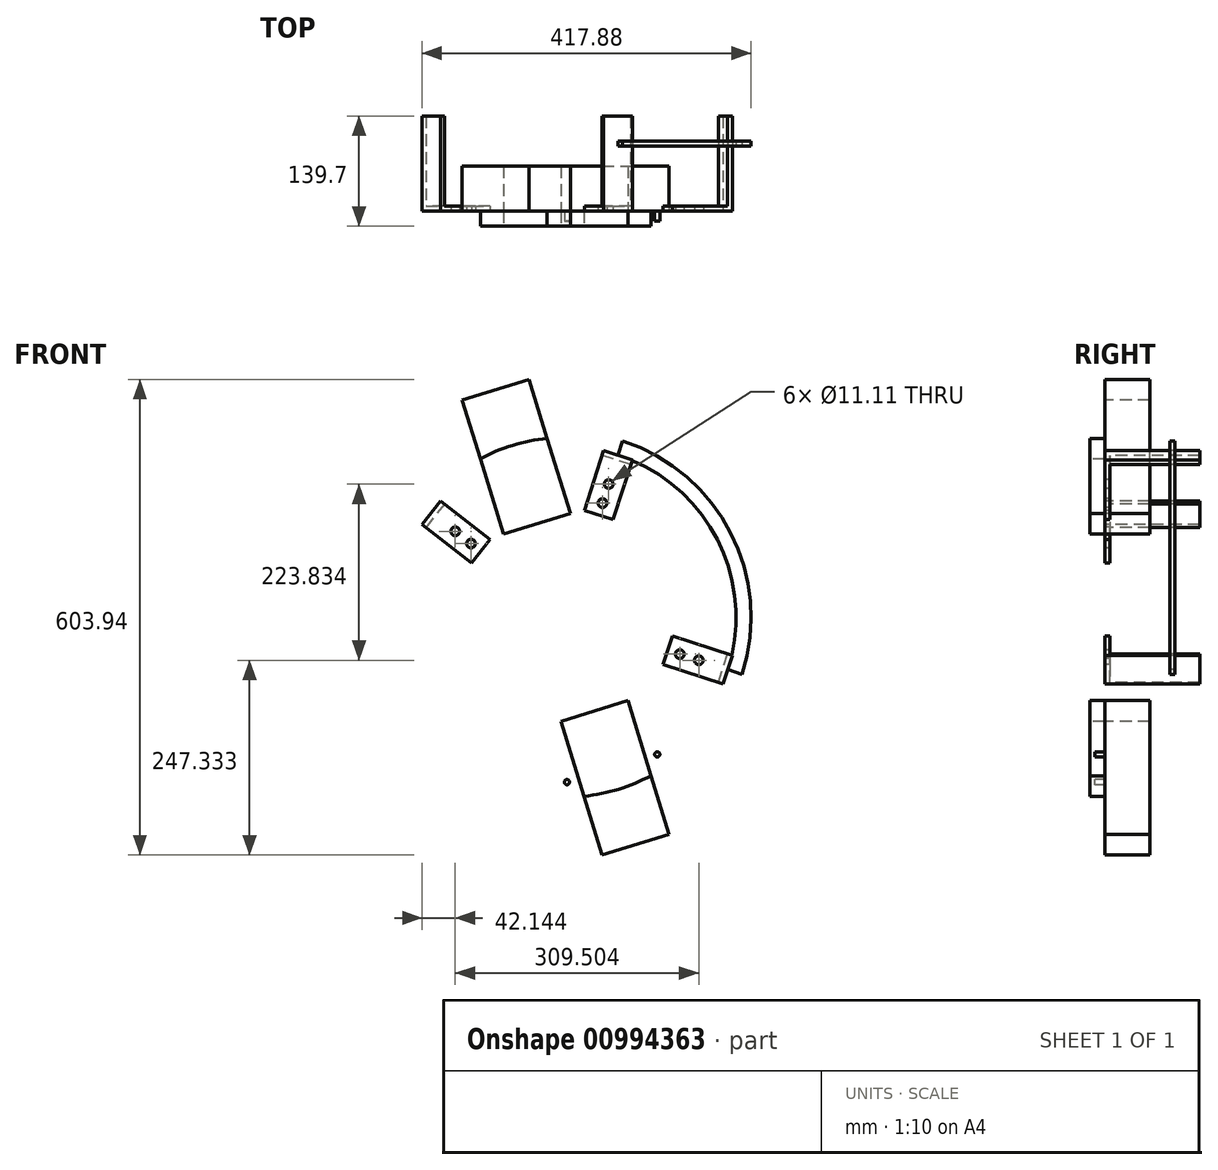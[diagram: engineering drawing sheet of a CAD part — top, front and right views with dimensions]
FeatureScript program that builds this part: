
annotation { "Feature Type Name" : "Feature", "Feature Type Description" : "" }
export const myFeature = defineFeature(function(context is Context, id is Id, definition is map)
    precondition{}
    {
        {
            var Q0;
            Q0=qCreatedBy(makeId("Front.planeOp"),FACE);
            var sketch = newSketch(context, id + "F0", { "sketchPlane" : qUnion([Q0])});
            skCircle(sketch, "E0", {"center": v(0, 0) * mm, "radius": 228.6 * mm});
            skSolve(sketch);
        }
        {
            var Q0;
            Q0=qSketchRegion(id+"F0",true);
            extrude(context, id + "F1", {"entities" : qUnion([Q0]), "depth" : 19.05 * mm, "offsetDistance" : 25.4 * mm});
        }
        {
            var Q0;
            Q0=makeQuery(id+"F1.opExtrude","CAP_FACE",FACE,{"disambiguationData":[OSD([sQuery(id+"F0.wireOp",EDGE,"E0")])],"isStart":false});
            var sketch = newSketch(context, id + "F2", { "sketchPlane" : qUnion([Q0])});
            skCircle(sketch, "E1", {"center": v(0, 0) * mm, "radius": 38.1 * mm});
            skSolve(sketch);
        }
        {
            var Q0;
            Q0=makeQuery(id+"F2.imprint","IMPRINT",FACE,{"disambiguationData":[TD([[makeQuery(id+"F2.imprint","IMPRINT",EDGE,{"derivedFrom":sQuery(id+"F2.wireOp",EDGE,"E1")}),1.0]])]});
            extrude(context, id + "F3", {"entities" : qUnion([Q0]), "operationType" : NewBodyOperationType.REMOVE, "endBound" : BoundingType.THROUGH_ALL, "oppositeDirection" : true, "depth" : 25.4 * mm, "offsetDistance" : 25.4 * mm});
        }
        {
            var Q0;
            Q0=makeQuery(id+"F1.opExtrude","CAP_FACE",FACE,{"disambiguationData":[OSD([sQuery(id+"F0.wireOp",EDGE,"E0")])],"isStart":false});
            var sketch = newSketch(context, id + "F4", { "sketchPlane" : qUnion([Q0])});
            skLineSegment(sketch, "E2", {"start": v(0, 0) * mm, "end": v(-180.4, 140.41) * mm, "construction": true});
            skCircle(sketch, "E3", {"center": v(-120.26, 93.6) * mm, "radius": 4.76 * mm});
            skCircle(sketch, "E4", {"center": v(-140.3, 109.21) * mm, "radius": 4.76 * mm});
            skLineSegment(sketch, "E5", {"start": v(0, 0) * mm, "end": v(-67.23, 218.49) * mm, "construction": true});
            skCircle(sketch, "E6", {"center": v(-116.36, 174.14) * mm, "radius": 3.3 * mm});
            skCircle(sketch, "E7", {"center": v(-1.67, 209.43) * mm, "radius": 3.3 * mm});
            skLineSegment(sketch, "E8", {"start": v(-1.67, 209.43) * mm, "end": v(-59.01, 191.79) * mm, "construction": true});
            skLineSegment(sketch, "E9", {"start": v(-59.01, 191.79) * mm, "end": v(-116.36, 174.14) * mm, "construction": true});
            skLineSegment(sketch, "E10", {"start": v(0, 0) * mm, "end": v(218.49, 67.23) * mm, "construction": true});
            skCircle(sketch, "E11.MirrorC", {"center": v(116.36, -174.14) * mm, "radius": 3.3 * mm});
            skCircle(sketch, "E12.MirrorC", {"center": v(1.67, -209.43) * mm, "radius": 3.3 * mm});
            skLineSegment(sketch, "E13.MirrorCS", {"start": v(59.01, -191.79) * mm, "end": v(1.67, -209.43) * mm, "construction": true});
            skLineSegment(sketch, "E14.MirrorCS", {"start": v(116.36, -174.14) * mm, "end": v(59.01, -191.79) * mm, "construction": true});
            skLineSegment(sketch, "E15", {"start": v(0, 0) * mm, "end": v(70.25, 217.54) * mm, "construction": true});
            skLineSegment(sketch, "E16", {"start": v(0, 0) * mm, "end": v(217.54, -70.25) * mm, "construction": true});
            skCircle(sketch, "E17", {"center": v(145.03, -46.83) * mm, "radius": 4.76 * mm});
            skCircle(sketch, "E18", {"center": v(169.2, -54.64) * mm, "radius": 4.76 * mm});
            skCircle(sketch, "E19", {"center": v(46.83, 145.03) * mm, "radius": 4.76 * mm});
            skCircle(sketch, "E20", {"center": v(54.64, 169.2) * mm, "radius": 4.76 * mm});
            skLineSegment(sketch, "E21", {"start": v(-79.09, 105.88) * mm, "end": v(5.88, 132.03) * mm});
            skLineSegment(sketch, "E22", {"start": v(5.88, 132.03) * mm, "end": v(-46.41, 301.97) * mm});
            skLineSegment(sketch, "E23", {"start": v(-46.41, 301.97) * mm, "end": v(-131.38, 275.82) * mm});
            skLineSegment(sketch, "E24", {"start": v(-131.38, 275.82) * mm, "end": v(-79.09, 105.88) * mm});
            skLineSegment(sketch, "E25", {"start": v(-36.6, 118.96) * mm, "end": v(-88.9, 288.9) * mm, "construction": true});
            skLineSegment(sketch, "E26.MirrorCS", {"start": v(-5.88, -132.03) * mm, "end": v(79.09, -105.88) * mm});
            skLineSegment(sketch, "E27.MirrorCS", {"start": v(79.09, -105.88) * mm, "end": v(131.38, -275.82) * mm});
            skLineSegment(sketch, "E28.MirrorCS", {"start": v(131.38, -275.82) * mm, "end": v(46.41, -301.97) * mm});
            skLineSegment(sketch, "E29.MirrorCS", {"start": v(46.41, -301.97) * mm, "end": v(-5.88, -132.03) * mm});
            skSolve(sketch);
        }
        {
            var Q0;
            Q0=makeQuery(id+"F4.imprint","IMPRINT",FACE,{"disambiguationData":[TD([[makeQuery(id+"F4.imprint","IMPRINT",EDGE,{"derivedFrom":sQuery(id+"F4.wireOp",EDGE,"E20")}),1.0]])]});
            var Q1;
            Q1=makeQuery(id+"F4.imprint","IMPRINT",FACE,{"disambiguationData":[TD([[makeQuery(id+"F4.imprint","IMPRINT",EDGE,{"derivedFrom":sQuery(id+"F4.wireOp",EDGE,"E19")}),1.0]])]});
            var Q2;
            Q2=makeQuery(id+"F4.imprint","IMPRINT",FACE,{"disambiguationData":[TD([[makeQuery(id+"F4.imprint","IMPRINT",EDGE,{"derivedFrom":sQuery(id+"F4.wireOp",EDGE,"E3")}),1.0]])]});
            var Q3;
            Q3=makeQuery(id+"F4.imprint","IMPRINT",FACE,{"disambiguationData":[TD([[makeQuery(id+"F4.imprint","IMPRINT",EDGE,{"derivedFrom":sQuery(id+"F4.wireOp",EDGE,"E4")}),1.0]])]});
            var Q4;
            Q4=makeQuery(id+"F4.imprint","IMPRINT",FACE,{"disambiguationData":[TD([[makeQuery(id+"F4.imprint","IMPRINT",EDGE,{"derivedFrom":sQuery(id+"F4.wireOp",EDGE,"E18")}),1.0]])]});
            var Q5;
            Q5=makeQuery(id+"F4.imprint","IMPRINT",FACE,{"disambiguationData":[TD([[makeQuery(id+"F4.imprint","IMPRINT",EDGE,{"derivedFrom":sQuery(id+"F4.wireOp",EDGE,"E17")}),1.0]])]});
            var Q6;
            Q6=makeQuery(id+"F4.imprint","IMPRINT",FACE,{"disambiguationData":[TD([[makeQuery(id+"F4.imprint","IMPRINT",EDGE,{"derivedFrom":sQuery(id+"F4.wireOp",EDGE,"E11.MirrorC")}),-1.0]])]});
            var Q7;
            Q7=makeQuery(id+"F4.imprint","IMPRINT",FACE,{"disambiguationData":[TD([[makeQuery(id+"F4.imprint","IMPRINT",EDGE,{"derivedFrom":sQuery(id+"F4.wireOp",EDGE,"E12.MirrorC")}),-1.0]])]});
            var Q8;
            Q8=makeQuery(id+"F4.imprint","IMPRINT",FACE,{"disambiguationData":[TD([[makeQuery(id+"F4.imprint","IMPRINT",EDGE,{"derivedFrom":sQuery(id+"F4.wireOp",EDGE,"E6")}),1.0]])]});
            var Q9;
            Q9=makeQuery(id+"F4.imprint","IMPRINT",FACE,{"disambiguationData":[TD([[makeQuery(id+"F4.imprint","IMPRINT",EDGE,{"derivedFrom":sQuery(id+"F4.wireOp",EDGE,"E7")}),1.0]])]});
            extrude(context, id + "F5", {"entities" : qUnion([Q0, Q1, Q2, Q3, Q4, Q5, Q6, Q7, Q8, Q9]), "operationType" : NewBodyOperationType.REMOVE, "endBound" : BoundingType.THROUGH_ALL, "oppositeDirection" : true, "depth" : 25.4 * mm, "offsetDistance" : 25.4 * mm});
        }
        {
            var Q0;
            Q0=makeQuery(id+"F1.opExtrude","CAP_FACE",FACE,{"disambiguationData":[OSD([sQuery(id+"F0.wireOp",EDGE,"E0")])],"isStart":false});
            var sketch = newSketch(context, id + "F6", { "sketchPlane" : qUnion([Q0])});
            skLineSegment(sketch, "E30", {"start": v(0, 0) * mm, "end": v(0, 228.6) * mm, "construction": true});
            skCircle(sketch, "E31", {"center": v(-120.26, 93.6) * mm, "radius": 10.8 * mm});
            skCircle(sketch, "E32", {"center": v(-140.3, 109.21) * mm, "radius": 10.8 * mm});
            skCircle(sketch, "E33", {"center": v(-1.67, 209.43) * mm, "radius": 9.53 * mm});
            skCircle(sketch, "E34", {"center": v(-116.36, 174.14) * mm, "radius": 9.53 * mm});
            skCircle(sketch, "E35.MirrorC", {"center": v(116.36, -174.14) * mm, "radius": 9.53 * mm});
            skCircle(sketch, "E36.MirrorC", {"center": v(1.67, -209.43) * mm, "radius": 9.53 * mm});
            skCircle(sketch, "E37", {"center": v(54.64, 169.2) * mm, "radius": 10.8 * mm});
            skCircle(sketch, "E38", {"center": v(46.83, 145.03) * mm, "radius": 10.8 * mm});
            skCircle(sketch, "E39", {"center": v(169.2, -54.64) * mm, "radius": 10.8 * mm});
            skCircle(sketch, "E40", {"center": v(145.03, -46.83) * mm, "radius": 10.8 * mm});
            skSolve(sketch);
        }
        {
            var Q0;
            Q0=qSketchRegion(id+"F6",true);
            extrude(context, id + "F7", {"entities" : qUnion([Q0]), "operationType" : NewBodyOperationType.REMOVE, "oppositeDirection" : true, "depth" : 6.35 * mm, "offsetDistance" : 25.4 * mm});
        }
        {
            var Q0;
            Q0=makeQuery(id+"F1.opExtrude","CAP_FACE",FACE,{"disambiguationData":[OSD([sQuery(id+"F0.wireOp",EDGE,"E0")])],"isStart":true});
            var sketch = newSketch(context, id + "F8", { "sketchPlane" : qUnion([Q0])});
            skLineSegment(sketch, "E41", {"start": v(-211.76, -48.36) * mm, "end": v(-135.62, -23.78) * mm});
            skLineSegment(sketch, "E42", {"start": v(-135.62, -23.78) * mm, "end": v(-123.91, -60.03) * mm});
            skLineSegment(sketch, "E43", {"start": v(-123.91, -60.03) * mm, "end": v(-200.05, -84.62) * mm});
            skLineSegment(sketch, "E44", {"start": v(-200.05, -84.62) * mm, "end": v(-211.76, -48.36) * mm});
            skLineSegment(sketch, "E45", {"start": v(-129.77, -41.9) * mm, "end": v(-205.9, -66.5) * mm, "construction": true});
            skCircle(sketch, "E46", {"center": v(-145.03, -46.83) * mm, "radius": 5.56 * mm});
            skCircle(sketch, "E47", {"center": v(-169.2, -54.64) * mm, "radius": 5.56 * mm});
            skSolve(sketch);
        }
        {
            var Q0;
            Q0=makeQuery(id+"F8.imprint","IMPRINT",FACE,{"disambiguationData":[TD([[makeQuery(id+"F8.imprint","IMPRINT",EDGE,{"derivedFrom":sQuery(id+"F8.wireOp",EDGE,"E41")}),-1.0]])]});
            extrude(context, id + "F9", {"entities" : qUnion([Q0]), "depth" : 6.35 * mm, "offsetDistance" : 25.4 * mm});
        }
        {
            var Q0;
            Q0=makeQuery(id+"F9.opExtrude","CAP_FACE",FACE,{"disambiguationData":[OSD([sQuery(id+"F8.wireOp",EDGE,"E41"),sQuery(id+"F8.wireOp",EDGE,"E42"),sQuery(id+"F8.wireOp",EDGE,"E43"),sQuery(id+"F8.wireOp",EDGE,"E44"),sQuery(id+"F8.wireOp",EDGE,"E46"),sQuery(id+"F8.wireOp",EDGE,"E47")])],"isStart":false});
            var sketch = newSketch(context, id + "F10", { "sketchPlane" : qUnion([Q0])});
            skLineSegment(sketch, "E48", {"start": v(-211.76, -48.36) * mm, "end": v(-200.05, -84.62) * mm});
            skLineSegment(sketch, "E49", {"start": v(-200.05, -84.62) * mm, "end": v(-194.01, -82.67) * mm});
            skLineSegment(sketch, "E50", {"start": v(-194.01, -82.67) * mm, "end": v(-205.72, -46.41) * mm});
            skLineSegment(sketch, "E51", {"start": v(-205.72, -46.41) * mm, "end": v(-211.76, -48.36) * mm});
            skSolve(sketch);
        }
        {
            var Q0;
            Q0=qSketchRegion(id+"F10",true);
            extrude(context, id + "F11", {"entities" : qUnion([Q0]), "operationType" : NewBodyOperationType.ADD, "depth" : 114.3 * mm, "offsetDistance" : 25.4 * mm});
        }
        {
            var Q0;
            Q0=qCreatedBy(makeId("Top.planeOp"),FACE);
            var sketch = newSketch(context, id + "F12", { "sketchPlane" : qUnion([Q0])});
            skLineSegment(sketch, "E52", {"start": v(0, 0) * mm, "end": v(0, 31.2) * mm});
            skSolve(sketch);
        }
        {
            var Q0;
            Q0=makeQuery(id+"F9.opExtrude","SWEPT_BODY",BODY,{"disambiguationData":[OSD([sQuery(id+"F8.wireOp",EDGE,"E41"),sQuery(id+"F8.wireOp",EDGE,"E42"),sQuery(id+"F8.wireOp",EDGE,"E43"),sQuery(id+"F8.wireOp",EDGE,"E44"),sQuery(id+"F8.wireOp",EDGE,"E46"),sQuery(id+"F8.wireOp",EDGE,"E47")])]});
            var Q1;
            Q1=sQuery(id+"F12.wireOp",EDGE,"E52");
            transform(context, id + "F13", {"entities" : qUnion([Q0]), "transformType" : TransformType.ROTATION, "transformAxis" : qUnion([Q1]), "angle" : 90 * degree, "oppositeDirection" : true, "makeCopy" : true});
        }
        {
            var Q0;
            Q0=makeQuery(id+"F13.opPattern","COPY",BODY,{"derivedFrom":makeQuery(id+"F9.opExtrude","SWEPT_BODY",BODY,{"disambiguationData":[OSD([sQuery(id+"F8.wireOp",EDGE,"E41"),sQuery(id+"F8.wireOp",EDGE,"E42"),sQuery(id+"F8.wireOp",EDGE,"E43"),sQuery(id+"F8.wireOp",EDGE,"E44"),sQuery(id+"F8.wireOp",EDGE,"E46"),sQuery(id+"F8.wireOp",EDGE,"E47")])]}),"instanceName":"1"});
            var Q1;
            Q1=sQuery(id+"F12.wireOp",EDGE,"E52");
            transform(context, id + "F14", {"entities" : qUnion([Q0]), "transformType" : TransformType.ROTATION, "transformAxis" : qUnion([Q1]), "angle" : 70 * degree, "oppositeDirection" : true, "makeCopy" : true});
        }
        {
            var Q0;
            Q0=makeQuery(id+"F1.opExtrude","CAP_FACE",FACE,{"disambiguationData":[OSD([sQuery(id+"F0.wireOp",EDGE,"E0")])],"isStart":true});
            var sketch = newSketch(context, id + "F15", { "sketchPlane" : qUnion([Q0])});
            skArc(sketch, "E53", {"start": v(-66.5, 205.9) * mm, "mid": v(-192.61, 98.58) * mm, "end": v(-205.9, -66.5) * mm});
            skArc(sketch, "E54", {"start": v(-72.35, 224.04) * mm, "mid": v(-209.57, 107.26) * mm, "end": v(-224.04, -72.35) * mm});
            skLineSegment(sketch, "E55", {"start": v(-224.04, -72.35) * mm, "end": v(-205.9, -66.5) * mm});
            skLineSegment(sketch, "E56", {"start": v(-66.5, 205.9) * mm, "end": v(-72.35, 224.04) * mm});
            skSolve(sketch);
        }
        {
            var Q0;
            Q0=qSketchRegion(id+"F15",true);
            extrude(context, id + "F16", {"entities" : qUnion([Q0]), "depth" : 88.9 * mm, "offsetDistance" : 25.4 * mm, "hasSecondDirection" : true, "secondDirectionOppositeDirection" : false, "secondDirectionDepth" : 82.55 * mm});
        }
        {
            var Q0;
            {var subQ0=sQuery(id+"F4.wireOp",EDGE,"E26.MirrorCS");Q0=makeQuery(id+"F4.imprint","IMPRINT",FACE,{"disambiguationData":[TD([[makeQuery(id+"F4.imprint","IMPRINT",EDGE,{"derivedFrom":subQ0}),-1.0]])]});}
            var Q1;
            {var subQ0=sQuery(id+"F4.wireOp",EDGE,"E21");Q1=makeQuery(id+"F4.imprint","IMPRINT",FACE,{"disambiguationData":[TD([[makeQuery(id+"F4.imprint","IMPRINT",EDGE,{"derivedFrom":subQ0}),1.0]])]});}
            var Q2;
            {var subQ0=sQuery(id+"F4.wireOp",EDGE,"E23");Q2=makeQuery(id+"F4.imprint","IMPRINT",FACE,{"disambiguationData":[TD([[makeQuery(id+"F4.imprint","IMPRINT",EDGE,{"derivedFrom":subQ0}),1.0]])]});}
            var Q3;
            {var subQ0=sQuery(id+"F4.wireOp",EDGE,"E28.MirrorCS");Q3=makeQuery(id+"F4.imprint","IMPRINT",FACE,{"disambiguationData":[TD([[makeQuery(id+"F4.imprint","IMPRINT",EDGE,{"derivedFrom":subQ0}),-1.0]])]});}
            extrude(context, id + "F17", {"entities" : qUnion([Q0, Q1, Q2, Q3]), "oppositeDirection" : true, "depth" : 76.2 * mm, "offsetDistance" : 25.4 * mm, "hasSecondDirection" : true, "secondDirectionOppositeDirection" : true, "secondDirectionDepth" : 19.05 * mm});
        }
    });
